# Revit family: result
name_source: partatom
category: Plumbing Fixtures
revit_build: Autodesk Revit 2015 (Build: 20140903_1530(x64)
units: mm (PartAtom-declared; Revit-internal decimal feet)

## types (1)
- Default
    BIMobject category = Basins
    BIMobject category code = sanitary-basins
    BIMobject main category = Sanitary
    BIMobject main category code = sanitary
    Brand url = http://www.duravit.com
    Edition number = 1
    GTIN code = https://4053424981970
    IFC Classification = Sanitary Terminal
    Installation instructions = https://pro.duravit.com
    Manufacturer name = DURAVIT
    Masterformat 2014 Code = 22 45 26
    Masterformat 2014 Description = Eye/Face Wash Equipment
    Material main = Ceramics
    NBS Reference Code = 31-76
    NBS Reference Description = Sanitary Dispensing And Disposal Units
    OmniClass Code = 23-21 43 23
    OmniClass Description = Sanitary Waste Receptacles
    Product Guid = 812e9b59-c0dc-4270-b1e4-00e3cad37c5e
    Product SKU = d-neo-sink-236780
    Product certification = https://pro.duravit.com
    Product data url = https://bimobject.com
    Product family = D-Neo
    Product group = Sinks
    Product name = 236780 D-Neo Sink
    Product url = https://pro.duravit.com
    QR code = http://bimobject.com
    UNSPSC Code = 301815
    Uniclass 1.4 Code = L721
    Uniclass 1.4 Description = Sanitary equipment
    Uniclass 2.0 Code = PR-31-76
    Uniclass 2.0 Description = Sanitary Dispensing And Disposal Units
    Uniclass 2015 Code = Pr_40_20_96
    Uniclass 2015 Name = Wash basins, sinks and troughs
    Uniformat II Code = E1010
    Uniformat II Description = Commercial Equipment

## geometry (parser evidence)
native form markers: Sweep x4
no freeform markers — native parametric forms only
